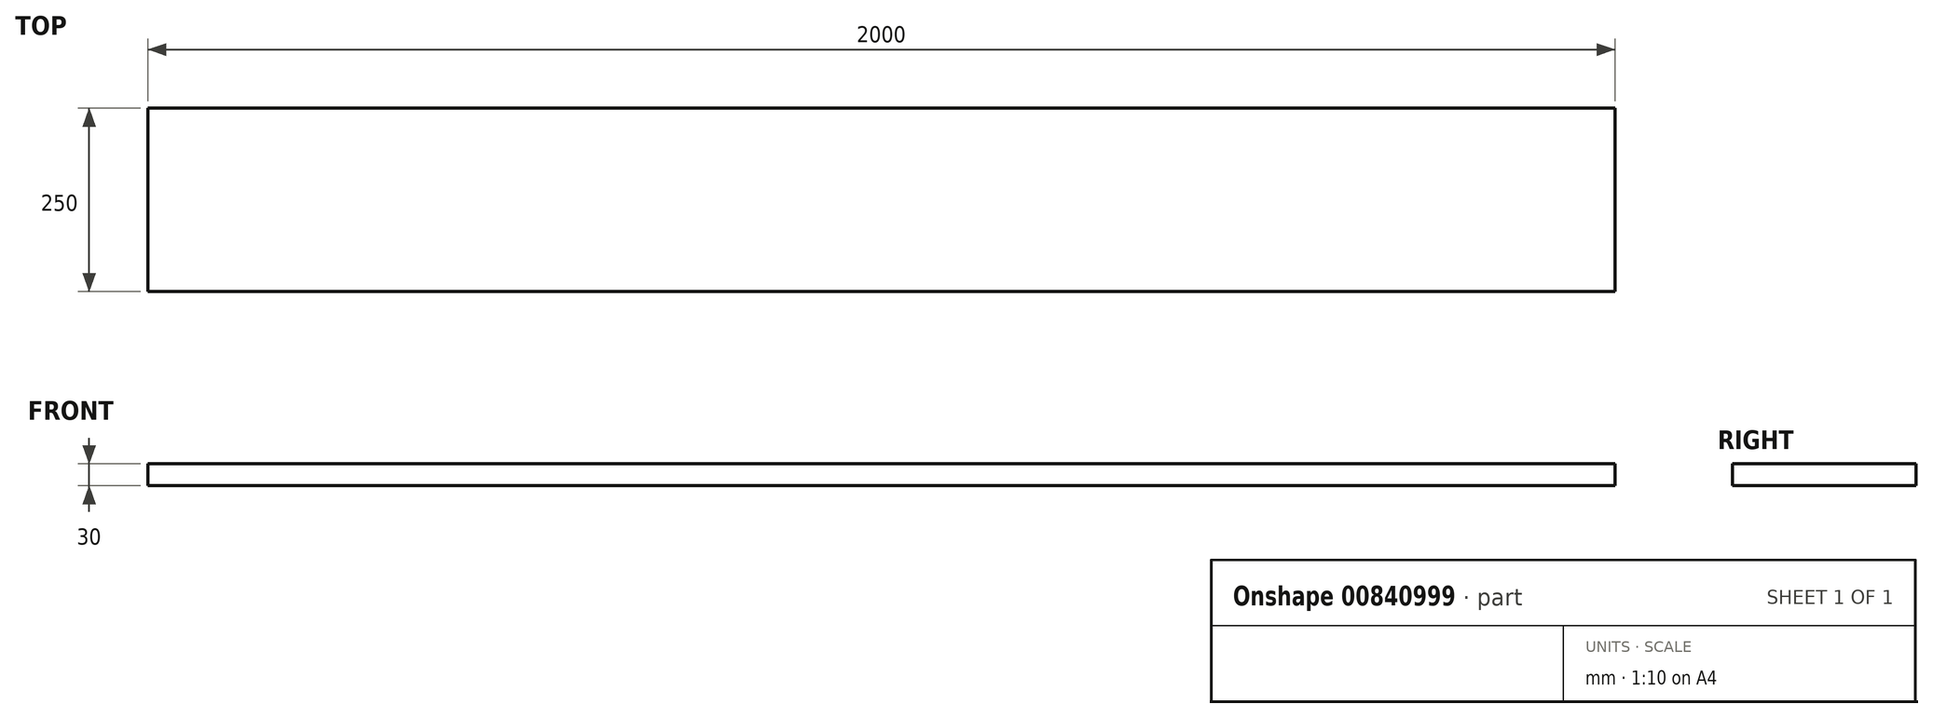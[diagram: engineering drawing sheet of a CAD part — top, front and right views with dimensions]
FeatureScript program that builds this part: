
annotation { "Feature Type Name" : "Feature", "Feature Type Description" : "" }
export const myFeature = defineFeature(function(context is Context, id is Id, definition is map)
    precondition{}
    {
        {
            var Q0;
            Q0=qCreatedBy(makeId("Top.planeOp"),FACE);
            var sketch = newSketch(context, id + "F0", { "sketchPlane" : qUnion([Q0])});
            skLineSegment(sketch, "E0.bottom", {"start": v(1000, -125) * mm, "end": v(-1000, -125) * mm});
            skLineSegment(sketch, "E0.top", {"start": v(1000, 125) * mm, "end": v(-1000, 125) * mm});
            skLineSegment(sketch, "E0.left", {"start": v(1000, -125) * mm, "end": v(1000, 125) * mm});
            skLineSegment(sketch, "E0.right", {"start": v(-1000, -125) * mm, "end": v(-1000, 125) * mm});
            skPoint(sketch, "E0.middle", {"position": v(0, 0) * mm});
            skSolve(sketch);
        }
        {
            var Q0;
            Q0 = qSketchRegion(id + "F0", true);
            extrude(context, id + "F1", {"entities" : qUnion([Q0]), "depth" : 30 * mm, "offsetDistance" : 25 * mm});
        }
    });
